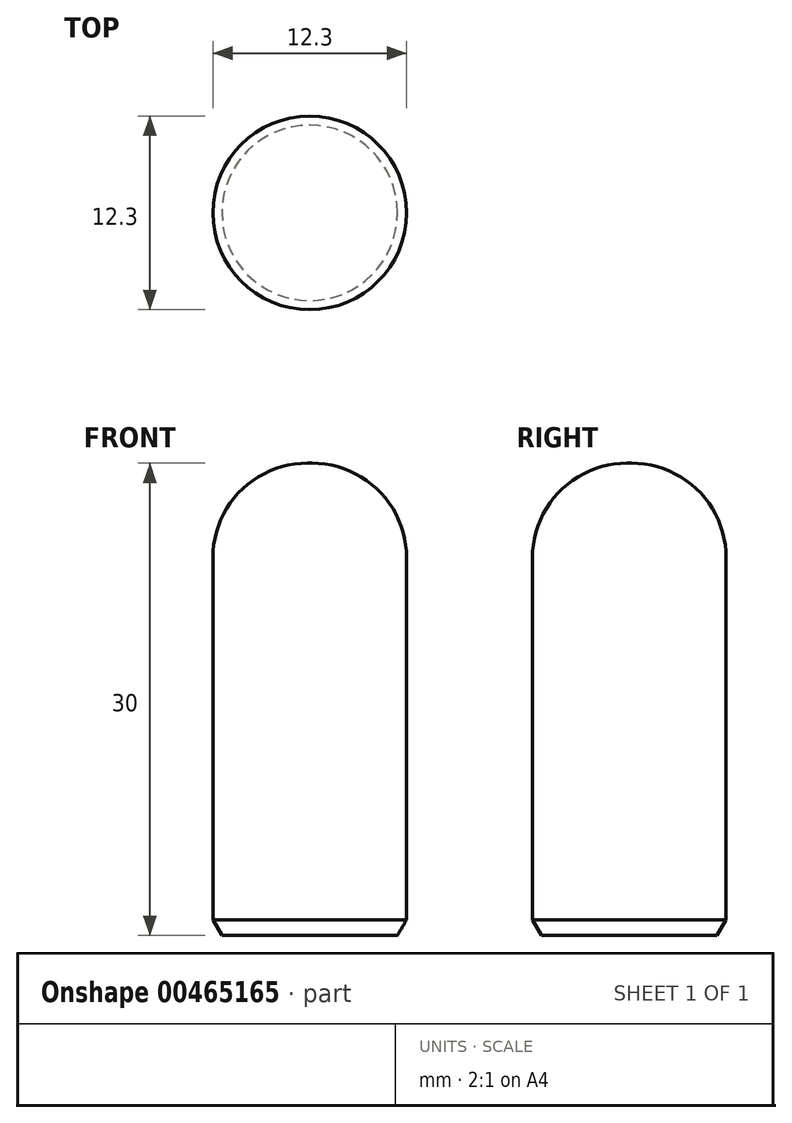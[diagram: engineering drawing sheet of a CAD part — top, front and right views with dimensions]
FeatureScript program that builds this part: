
annotation { "Feature Type Name" : "Feature", "Feature Type Description" : "" }
export const myFeature = defineFeature(function(context is Context, id is Id, definition is map)
    precondition{}
    {
        {
            var Q0;
            Q0=qCreatedBy(makeId("Top.planeOp"),FACE);
            var sketch = newSketch(context, id + "F0", { "sketchPlane" : qUnion([Q0])});
            skCircle(sketch, "E0", {"center": v(0, 0) * mm, "radius": 6.15 * mm});
            skSolve(sketch);
        }
        {
            var Q0;
            Q0 = qSketchRegion(id + "F0", true);
            extrude(context, id + "F1", {"entities" : qUnion([Q0]), "depth" : 30 * mm});
        }
        {
            var Q0;
            Q0=makeQuery(id+"F1.opExtrude","CAP_EDGE",EDGE,{"disambiguationData":[OSD([sQuery(id+"F0.wireOp",EDGE,"E0")])],"isStart":false});
            fillet(context, id + "F2", {"entities" : qUnion([Q0]), "radius" : 6 * mm, "tangentPropagation" : true, "allowEdgeOverflow" : false});
        }
        {
            var Q0;
            Q0=makeQuery(id+"F1.opExtrude","CAP_EDGE",EDGE,{"disambiguationData":[OSD([sQuery(id+"F0.wireOp",EDGE,"E0")])],"isStart":true});
            chamfer(context, id + "F3", {"entities" : qUnion([Q0]), "chamferType" : ChamferType.OFFSET_ANGLE, "width" : 1 * mm, "oppositeDirection" : false, "angle" : 30 * degree, "tangentPropagation" : true});
        }
    });
